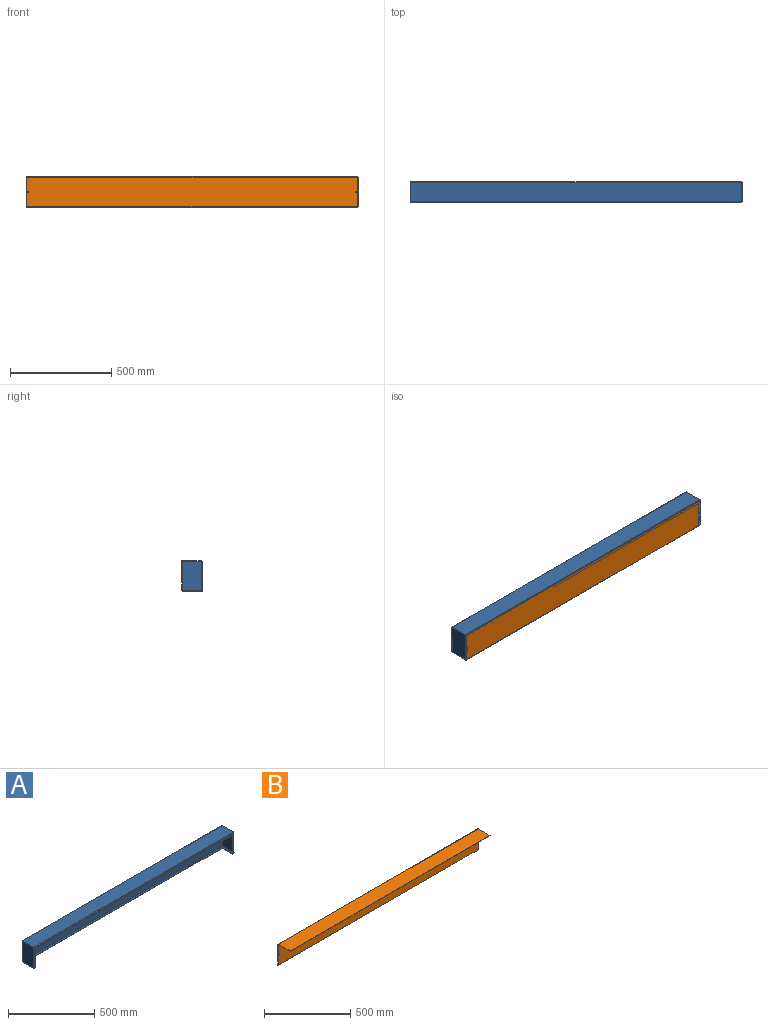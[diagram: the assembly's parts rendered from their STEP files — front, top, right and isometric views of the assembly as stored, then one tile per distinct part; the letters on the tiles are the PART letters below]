
ASSEMBLY  parts=2 mates=1
PART A: 90 faces, bbox 1640x100x150 mm
  f0: plane 2x0.01mm, normal (0,0,-1), area 0mm2, adj f2,f3,f9,f33
  f1: plane 2x0.01mm, normal (0,0,-1), area 0mm2, adj f2,f3,f10,f51
  f2: plane 1632x142mm, normal (0,1,0), area 231744mm2, adj f0,f1,f11,f30,f34,f53
  f3: plane 1632x142mm, normal (0,-1,0), area 231744mm2, adj f0,f1,f12,f31,f35,f54
  f4: plane 1609.97x2mm, normal (0,-1,0), area 3219.9mm2, adj f5,f6,f7,f8
  f5: plane 11x11mm, normal (-0.71,-0.71,0), area 31.1mm2, adj f4,f7,f8,f10
  f6: plane 11x11mm, normal (0.71,-0.71,0), area 31.1mm2, adj f4,f7,f8,f9
  f7: plane 1631.97x11mm, normal (0,0,-1), area 17830.7mm2, adj f4,f5,f6,f11
  f8: plane 1631.97x11mm, normal (0,0,1), area 17830.7mm2, adj f4,f5,f6,f12
  f9: plane 4x4mm, normal (1,0,0), area 9.4mm2, adj f0,f6,f11,f12
  f10: plane 4x4mm, normal (-1,0,0), area 9.4mm2, adj f1,f5,f11,f12
  f11: cylinder r=4mm len=1631.97mm, axis (1,0,0), area 10254mm2, adj f2,f7,f9,f10
  f12: cylinder r=2mm len=1631.97mm, axis (1,0,0), area 5127mm2, adj f3,f8,f9,f10
  f13: plane 2x1.98mm, normal (0,1,0), area 4mm2, adj f14,f17,f18,f29
  f14: plane 92x2mm, normal (1,0,0), area 184mm2, adj f13,f17,f18,f25
  f15: plane 2x1.98mm, normal (0,1,0), area 4mm2, adj f16,f17,f18,f28
  f16: plane 92x2mm, normal (-1,0,0), area 184mm2, adj f15,f17,f18,f24
  f17: plane 1635.96x92mm, normal (0,0,1), area 150508.3mm2, adj f13,f14,f15,f16,f26,f30
  f18: plane 1635.96x92mm, normal (0,0,-1), area 150508.3mm2, adj f13,f14,f15,f16,f27,f31
  f19: plane 1609.97x2mm, normal (0,0,-1), area 3219.9mm2, adj f20,f21,f22,f23
  f20: plane 11x11mm, normal (0.71,0,-0.71), area 31.1mm2, adj f19,f22,f23,f25
  f21: plane 11x11mm, normal (-0.71,0,-0.71), area 31.1mm2, adj f19,f22,f23,f24
  f22: plane 1631.97x11mm, normal (0,-1,0), area 17830.7mm2, adj f19,f20,f21,f26
  f23: plane 1631.97x11mm, normal (0,1,0), area 17830.7mm2, adj f19,f20,f21,f27
  f24: bspline ~4x4mm, area 10.4mm2, adj f16,f21,f26,f27
  f25: bspline ~4x4mm, area 10.5mm2, adj f14,f20,f26,f27
  f26: cylinder r=4mm len=1635.96mm, axis (-1,0,0), area 10269.9mm2, adj f17,f22,f24,f25
  f27: cylinder r=2mm len=1635.96mm, axis (-1,0,0), area 5135mm2, adj f18,f23,f24,f25
  f28: plane 4x4mm, normal (-1,0,0), area 9.4mm2, adj f15,f30,f31,f52
  f29: plane 4x4mm, normal (1,0,0), area 9.4mm2, adj f13,f30,f31,f32
  f30: cylinder r=4mm len=1632mm, axis (-1,0,0), area 10254.2mm2, adj f2,f17,f28,f29
  f31: cylinder r=2mm len=1632mm, axis (-1,0,0), area 5127.1mm2, adj f3,f18,f28,f29
  f32: plane 4x4mm, normal (0,0,1), area 9.4mm2, adj f29,f34,f35,f37
  f33: plane 4x4mm, normal (0,0,-1), area 9.4mm2, adj f0,f34,f35,f36
  f34: cylinder r=4mm len=142mm, axis (0,0,1), area 892.2mm2, adj f2,f32,f33,f39
  f35: cylinder r=2mm len=142mm, axis (0,0,1), area 446.1mm2, adj f3,f32,f33,f40
  f36: plane 2x0.01mm, normal (0,0,-1), area 0mm2, adj f33,f39,f40,f48
  f37: plane 2x1.98mm, normal (0,1,0), area 4mm2, adj f32,f38,f39,f40
  f38: plane 92x2mm, normal (0,0,1), area 184mm2, adj f37,f39,f40,f61
  f39: plane 143.98x92mm, normal (1,0,0), area 13246.2mm2, adj f34,f36,f37,f38,f49,f63
  f40: plane 143.98x92mm, normal (-1,0,0), area 13246.2mm2, adj f35,f36,f37,f38,f50,f64
  f41: plane 82.97x2mm, normal (-1,0,0), area 165.9mm2, adj f42,f44,f45,f46
  f42: plane 11x11mm, normal (-0.71,0.71,0), area 31.1mm2, adj f41,f45,f46,f48
  f43: plane 2x1.98mm, normal (1,0,0), area 4mm2, adj f44,f45,f46,f47
  f44: plane 11x2mm, normal (0,-1,0), area 22mm2, adj f41,f43,f45,f46
  f45: plane 93.97x11mm, normal (0,0,-1), area 973.1mm2, adj f41,f42,f43,f44,f49
  f46: plane 93.97x11mm, normal (0,0,1), area 973.1mm2, adj f41,f42,f43,f44,f50
  f47: plane 4x4mm, normal (0,-1,0), area 9.4mm2, adj f43,f49,f50,f62
  f48: plane 4x4mm, normal (0,1,0), area 9.4mm2, adj f36,f42,f49,f50
  f49: cylinder r=4mm len=91.99mm, axis (0,-1,0), area 578mm2, adj f39,f45,f47,f48
  f50: cylinder r=2mm len=91.99mm, axis (0,-1,0), area 289mm2, adj f40,f46,f47,f48
  f51: plane 4x4mm, normal (0,0,-1), area 9.4mm2, adj f1,f53,f54,f66
  f52: plane 4x4mm, normal (0,0,1), area 9.4mm2, adj f28,f53,f54,f65
  f53: cylinder r=4mm len=142mm, axis (0,0,-1), area 892.2mm2, adj f2,f51,f52,f68
  f54: cylinder r=2mm len=142mm, axis (0,0,-1), area 446.1mm2, adj f3,f51,f52,f69
  f55: plane 2x1.98mm, normal (1,0,0), area 4mm2, adj f57,f59,f60,f62
  f56: plane 132.97x2mm, normal (-1,0,0), area 265.9mm2, adj f57,f58,f59,f60
  f57: plane 11x2mm, normal (0,0,-1), area 22mm2, adj f55,f56,f59,f60
  f58: plane 11x11mm, normal (-0.71,0,0.71), area 31.1mm2, adj f56,f59,f60,f61
  f59: plane 143.97x11mm, normal (0,-1,0), area 1523.1mm2, adj f55,f56,f57,f58,f63
  f60: plane 143.97x11mm, normal (0,1,0), area 1523.1mm2, adj f55,f56,f57,f58,f64
  f61: bspline ~4x4mm, area 10.4mm2, adj f38,f58,f63,f64
  f62: plane 4x4mm, normal (0,0,-1), area 9.4mm2, adj f47,f55,f63,f64
  f63: cylinder r=4mm len=143.98mm, axis (0,0,1), area 900.1mm2, adj f39,f59,f61,f62
  f64: cylinder r=2mm len=143.98mm, axis (0,0,1), area 450mm2, adj f40,f60,f61,f62
  f65: plane 2x1.98mm, normal (0,1,0), area 4mm2, adj f52,f67,f68,f69
  f66: plane 2x0.01mm, normal (0,0,-1), area 0mm2, adj f51,f68,f69,f76
  f67: plane 92x2mm, normal (0,0,1), area 184mm2, adj f65,f68,f69,f87
  f68: plane 143.98x92mm, normal (-1,0,0), area 13246.2mm2, adj f53,f65,f66,f67,f78,f88
  f69: plane 143.98x92mm, normal (1,0,0), area 13246.2mm2, adj f54,f65,f66,f67,f79,f89
  f70: plane 2x1.98mm, normal (-1,0,0), area 4mm2, adj f72,f74,f75,f77
  f71: plane 82.97x2mm, normal (1,0,0), area 165.9mm2, adj f72,f73,f74,f75
  f72: plane 11x2mm, normal (0,-1,0), area 22mm2, adj f70,f71,f74,f75
  f73: plane 11x11mm, normal (0.71,0.71,0), area 31.1mm2, adj f71,f74,f75,f76
  f74: plane 93.97x11mm, normal (0,0,-1), area 973.1mm2, adj f70,f71,f72,f73,f78
  f75: plane 93.97x11mm, normal (0,0,1), area 973.1mm2, adj f70,f71,f72,f73,f79
  f76: plane 4x4mm, normal (0,1,0), area 9.4mm2, adj f66,f73,f78,f79
  f77: plane 4x4mm, normal (0,-1,0), area 9.4mm2, adj f70,f78,f79,f86
  f78: cylinder r=4mm len=91.99mm, axis (0,1,0), area 578mm2, adj f68,f74,f76,f77
  f79: cylinder r=2mm len=91.99mm, axis (0,1,0), area 289mm2, adj f69,f75,f76,f77
  f80: plane 132.97x2mm, normal (1,0,0), area 265.9mm2, adj f81,f83,f84,f85
  f81: plane 11x11mm, normal (0.71,0,0.71), area 31.1mm2, adj f80,f84,f85,f87
  f82: plane 2x1.98mm, normal (-1,0,0), area 4mm2, adj f83,f84,f85,f86
  f83: plane 11x2mm, normal (0,0,-1), area 22mm2, adj f80,f82,f84,f85
  f84: plane 143.97x11mm, normal (0,-1,0), area 1523.1mm2, adj f80,f81,f82,f83,f88
  f85: plane 143.97x11mm, normal (0,1,0), area 1523.1mm2, adj f80,f81,f82,f83,f89
  f86: plane 4x4mm, normal (0,0,-1), area 9.4mm2, adj f77,f82,f88,f89
  f87: bspline ~4x4mm, area 10.5mm2, adj f67,f81,f88,f89
  f88: cylinder r=4mm len=143.98mm, axis (0,0,-1), area 900.1mm2, adj f68,f84,f86,f87
  f89: cylinder r=2mm len=143.98mm, axis (0,0,-1), area 450mm2, adj f69,f85,f86,f87
PART B: 16 faces, bbox 1634x100x150 mm
  f0: plane 1634x2mm, normal (0,0,-1), area 3268mm2, adj f1,f4,f5,f6
  f1: plane 146x2mm, normal (-1,0,0), area 292mm2, adj f0,f5,f6,f13
  f2: cylinder r=3mm len=6mm, axis (0,-1,0), area 37.7mm2, adj f5,f6
  f3: cylinder r=3mm len=6mm, axis (0,-1,0), area 37.7mm2, adj f5,f6
  f4: plane 146x2mm, normal (1,0,0), area 292mm2, adj f0,f5,f6,f12
  f5: plane 1634x146mm, normal (0,1,0), area 238507.5mm2, adj f0,f1,f2,f3,f4,f14
  f6: plane 1634x146mm, normal (0,-1,0), area 238507.5mm2, adj f0,f1,f2,f3,f4,f15
  f7: plane 1634x2mm, normal (0,-1,0), area 3268mm2, adj f8,f9,f10,f11
  f8: plane 96x2mm, normal (1,0,0), area 192mm2, adj f7,f10,f11,f12
  f9: plane 96x2mm, normal (-1,0,0), area 192mm2, adj f7,f10,f11,f13
  f10: plane 1634x96mm, normal (0,0,1), area 156864mm2, adj f7,f8,f9,f14
  f11: plane 1634x96mm, normal (0,0,-1), area 156864mm2, adj f7,f8,f9,f15
  f12: plane 4x4mm, normal (1,0,0), area 9.4mm2, adj f4,f8,f14,f15
  f13: plane 4x4mm, normal (-1,0,0), area 9.4mm2, adj f1,f9,f14,f15
  f14: cylinder r=4mm len=1634mm, axis (1,0,0), area 10266.7mm2, adj f5,f10,f12,f13
  f15: cylinder r=2mm len=1634mm, axis (1,0,0), area 5133.4mm2, adj f6,f11,f12,f13
PLACE A t=(-297.05,-181.53,-82.44)mm
PLACE B rot(axis=(-1,0,0),180deg) t=(-297.05,-283.54,-84.44)mm
MATE fastened B.f11 <-> A.f7  axis (0,0,1) through (518.95,-183.54,-158.44)mm
